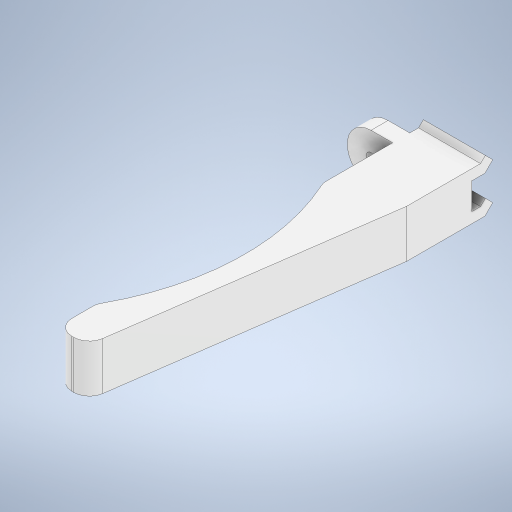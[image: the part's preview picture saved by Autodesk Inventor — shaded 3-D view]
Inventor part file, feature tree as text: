
AUTODESK INVENTOR PART (.ipt)
format: ipt  version: 2024 (Build 280153000, 153)  size: 618,496 bytes
history: native  units: in
note: dims shown in document units (in); Inventor stores cm internally (conversion verified against a paired STEP export)
features: other x1, fillet x1
ambient origin geometry x8: Origin, YZ Plane, XZ Plane, XY Plane, X Axis, Y Axis, Z Axis, Center Point
bodies: Solid2 (feature_tree)
feature tree (2):
  other  "Plane1"
  fillet  "Fillet1"  [1 undecoded]
note: 1 required parameter value undecoded (feature->parameter linkage not recoverable at this tier; creation-order binding heuristic only, values carry confidence <= 0.55)
